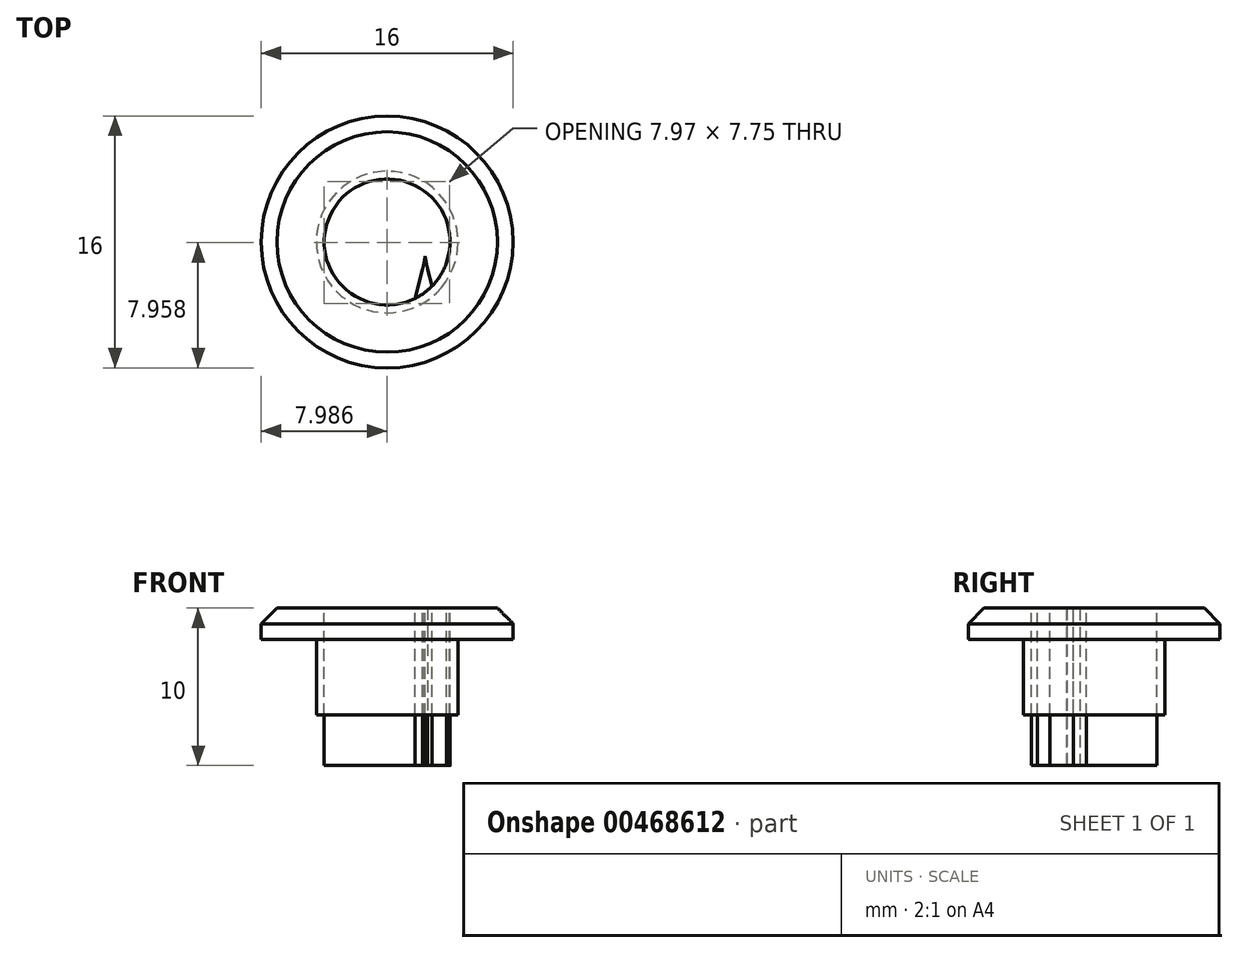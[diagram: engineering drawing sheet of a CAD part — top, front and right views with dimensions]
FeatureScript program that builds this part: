
annotation { "Feature Type Name" : "Feature", "Feature Type Description" : "" }
export const myFeature = defineFeature(function(context is Context, id is Id, definition is map)
    precondition{}
    {
        {
            var Q0;
            Q0=qCreatedBy(makeId("Top.planeOp"),FACE);
            var sketch = newSketch(context, id + "F0", { "sketchPlane" : qUnion([Q0])});
            skCircle(sketch, "E0", {"center": v(0, 0) * mm, "radius": 4 * mm});
            skCircle(sketch, "E1", {"center": v(0, 0) * mm, "radius": 8 * mm});
            skPoint(sketch, "E2", {"position": v(4.15, 5.67) * mm});
            skPoint(sketch, "E3.1.0", {"position": v(-5.11, 4.67) * mm});
            skPoint(sketch, "E3.2.0", {"position": v(-4.11, -4.59) * mm});
            skPoint(sketch, "E3.3.0", {"position": v(5.14, -3.59) * mm});
            skPoint(sketch, "E3.center", {"position": v(0.02, 0.54) * mm});
            skText(sketch, "E4", { "text": "N", "fontName": "OpenSans-Bold.ttf"});
            skText(sketch, "E5", { "text": "W", "fontName": "OpenSans-Bold.ttf"});
            skCircle(sketch, "E6", {"center": v(0, 0) * mm, "radius": 4.5 * mm});
            const initialGuessF0  = {"E4": [-0.00511, 0, 1, 0, 0.00467], "E5": [0, -0.00359, 1, 0, 0.00359]};
            skSetInitialGuess(sketch, initialGuessF0);
            skSolve(sketch);
        }
        {
            var Q0;
            Q0=qSketchRegion(id+"F0",true);
            var Q1;
            {var subQ10=sQuery(id+"F0.wireOp",EDGE,"E5.sketch_text.stroke-0");Q1=makeQuery(id+"F0.imprint","IMPRINT",FACE,{"disambiguationData":[TD([[makeQuery(id+"F0.imprint","IMPRINT",EDGE,{"derivedFrom":subQ10}),-1.0]])]});}
            var Q2;
            {var subQ0=sQuery(id+"F0.wireOp",EDGE,"E5.sketch_text.stroke-18");Q2=makeQuery(id+"F0.imprint","IMPRINT",FACE,{"disambiguationData":[TD([[makeQuery(id+"F0.imprint","IMPRINT",EDGE,{"derivedFrom":subQ0}),1.0]])]});}
            var Q3;
            {var subQ0=sQuery(id+"F0.wireOp",EDGE,"E4.sketch_text.stroke-2");Q3=makeQuery(id+"F0.imprint","IMPRINT",FACE,{"disambiguationData":[TD([[makeQuery(id+"F0.imprint","IMPRINT",EDGE,{"derivedFrom":subQ0}),-1.0]])]});}
            var Q4;
            {var subQ5=sQuery(id+"F0.wireOp",EDGE,"E4.sketch_text.stroke-12");Q4=makeQuery(id+"F0.imprint","IMPRINT",FACE,{"disambiguationData":[TD([[makeQuery(id+"F0.imprint","IMPRINT",EDGE,{"derivedFrom":subQ5}),-1.0]])]});}
            var Q5;
            {var subQ1=sQuery(id+"F0.wireOp",EDGE,"E4.sketch_text.stroke-2");Q5=makeQuery(id+"F0.imprint","IMPRINT",FACE,{"disambiguationData":[TD([[makeQuery(id+"F0.imprint","IMPRINT",EDGE,{"derivedFrom":subQ1}),1.0]])]});}
            extrude(context, id + "F1", {"entities" : qUnion([Q0, Q1, Q2, Q3, Q4, Q5]), "oppositeDirection" : true, "depth" : 2 * mm});
        }
        {
            var Q0;
            {var subQ15=sQuery(id+"F0.wireOp",EDGE,"E4.sketch_text.stroke-0");Q0=makeQuery(id+"F0.imprint","IMPRINT",FACE,{"disambiguationData":[TD([[makeQuery(id+"F0.imprint","IMPRINT",EDGE,{"derivedFrom":subQ15}),1.0]])]});}
            var Q1;
            {var subQ0=sQuery(id+"F0.wireOp",EDGE,"E4.sketch_text.stroke-4");var subQ1=sQuery(id+"F0.wireOp",EDGE,"E0");var subQ2=makeQuery(id+"F0.imprint","INTERSECT",VERTEX,{"derivedFrom":[subQ1,subQ0]});Q1=makeQuery(id+"F0.imprint","IMPRINT",FACE,{"disambiguationData":[TD([[makeQuery(id+"F0.imprint","IMPRINT",EDGE,{"disambiguationData":[TD([[subQ2,-1.0]])],"derivedFrom":subQ1}),1.0]])]});}
            var Q2;
            {var subQ1=sQuery(id+"F0.wireOp",EDGE,"E4.sketch_text.stroke-9");Q2=makeQuery(id+"F0.imprint","IMPRINT",FACE,{"disambiguationData":[TD([[makeQuery(id+"F0.imprint","IMPRINT",EDGE,{"derivedFrom":subQ1}),1.0]])]});}
            var Q3;
            {var subQ5=sQuery(id+"F0.wireOp",EDGE,"E5.sketch_text.stroke-2");Q3=makeQuery(id+"F0.imprint","IMPRINT",FACE,{"disambiguationData":[TD([[makeQuery(id+"F0.imprint","IMPRINT",EDGE,{"derivedFrom":subQ5}),-1.0]])]});}
            var Q4;
            {var subQ0=sQuery(id+"F0.wireOp",EDGE,"E4.sketch_text.stroke-0");Q4=makeQuery(id+"F0.imprint","IMPRINT",FACE,{"disambiguationData":[TD([[makeQuery(id+"F0.imprint","IMPRINT",EDGE,{"derivedFrom":subQ0}),-1.0]])]});}
            extrude(context, id + "F2", {"entities" : qUnion([Q0, Q1, Q2, Q3, Q4]), "operationType" : NewBodyOperationType.ADD, "oppositeDirection" : true, "depth" : 10 * mm});
        }
        {
            var Q0;
            Q0=makeQuery(id+"F1.opExtrude","CAP_EDGE",EDGE,{"disambiguationData":[OSD([sQuery(id+"F0.wireOp",EDGE,"E1")])],"isStart":true});
            chamfer(context, id + "F3", {"entities" : qUnion([Q0]), "width" : 1 * mm, "tangentPropagation" : true});
        }
        {
            var Q0;
            {var subQ0=sQuery(id+"F0.wireOp",EDGE,"E5.sketch_text.stroke-20");Q0=makeQuery(id+"F0.imprint","IMPRINT",FACE,{"disambiguationData":[TD([[makeQuery(id+"F0.imprint","IMPRINT",EDGE,{"derivedFrom":subQ0}),-1.0]])]});}
            var Q1;
            {var subQ0=sQuery(id+"F0.wireOp",EDGE,"E5.sketch_text.stroke-20");Q1=makeQuery(id+"F0.imprint","IMPRINT",FACE,{"disambiguationData":[TD([[makeQuery(id+"F0.imprint","IMPRINT",EDGE,{"derivedFrom":subQ0}),1.0]])]});}
            var Q2;
            {var subQ5=sQuery(id+"F0.wireOp",EDGE,"E0");var subQ7=sQuery(id+"F0.wireOp",EDGE,"E5.sketch_text.stroke-1");var subQ8=makeQuery(id+"F0.imprint","INTERSECT",VERTEX,{"derivedFrom":[subQ5,subQ7]});Q2=makeQuery(id+"F0.imprint","IMPRINT",FACE,{"disambiguationData":[TD([[makeQuery(id+"F0.imprint","IMPRINT",EDGE,{"disambiguationData":[TD([[subQ8,-1.0]])],"derivedFrom":subQ5}),-1.0]])]});}
            var Q3;
            {var subQ0=sQuery(id+"F0.wireOp",EDGE,"E4.sketch_text.stroke-5");var subQ1=sQuery(id+"F0.wireOp",EDGE,"E0");var subQ2=makeQuery(id+"F0.imprint","INTERSECT",VERTEX,{"derivedFrom":[subQ1,subQ0]});Q3=makeQuery(id+"F0.imprint","IMPRINT",FACE,{"disambiguationData":[TD([[makeQuery(id+"F0.imprint","IMPRINT",EDGE,{"disambiguationData":[TD([[subQ2,-1.0]])],"derivedFrom":subQ1}),-1.0]])]});}
            var Q4;
            {var subQ5=sQuery(id+"F0.wireOp",EDGE,"E0");var subQ7=sQuery(id+"F0.wireOp",EDGE,"E4.sketch_text.stroke-13");var subQ8=makeQuery(id+"F0.imprint","INTERSECT",VERTEX,{"derivedFrom":[subQ5,subQ7]});Q4=makeQuery(id+"F0.imprint","IMPRINT",FACE,{"disambiguationData":[TD([[makeQuery(id+"F0.imprint","IMPRINT",EDGE,{"disambiguationData":[TD([[subQ8,1.0]])],"derivedFrom":subQ5}),-1.0]])]});}
            var Q5;
            {var subQ0=sQuery(id+"F0.wireOp",EDGE,"E4.sketch_text.stroke-11");var subQ1=sQuery(id+"F0.wireOp",EDGE,"E0");var subQ2=makeQuery(id+"F0.imprint","INTERSECT",VERTEX,{"derivedFrom":[subQ1,subQ0]});Q5=makeQuery(id+"F0.imprint","IMPRINT",FACE,{"disambiguationData":[TD([[makeQuery(id+"F0.imprint","IMPRINT",EDGE,{"disambiguationData":[TD([[subQ2,1.0]])],"derivedFrom":subQ1}),-1.0]])]});}
            var Q6;
            {var subQ0=sQuery(id+"F0.wireOp",EDGE,"E4.sketch_text.stroke-11");var subQ1=sQuery(id+"F0.wireOp",EDGE,"E0");var subQ2=makeQuery(id+"F0.imprint","INTERSECT",VERTEX,{"derivedFrom":[subQ1,subQ0]});Q6=makeQuery(id+"F0.imprint","IMPRINT",FACE,{"disambiguationData":[TD([[makeQuery(id+"F0.imprint","IMPRINT",EDGE,{"disambiguationData":[TD([[subQ2,-1.0]])],"derivedFrom":subQ1}),-1.0]])]});}
            var Q7;
            {var subQ0=sQuery(id+"F0.wireOp",EDGE,"E4.sketch_text.stroke-8");var subQ1=sQuery(id+"F0.wireOp",EDGE,"E0");var subQ2=makeQuery(id+"F0.imprint","INTERSECT",VERTEX,{"derivedFrom":[subQ1,subQ0]});Q7=makeQuery(id+"F0.imprint","IMPRINT",FACE,{"disambiguationData":[TD([[makeQuery(id+"F0.imprint","IMPRINT",EDGE,{"disambiguationData":[TD([[subQ2,-1.0]])],"derivedFrom":subQ1}),-1.0]])]});}
            var Q8;
            {var subQ1=sQuery(id+"F0.wireOp",EDGE,"E0");var subQ5=sQuery(id+"F0.wireOp",EDGE,"E4.sketch_text.stroke-4");var subQ8=makeQuery(id+"F0.imprint","INTERSECT",VERTEX,{"derivedFrom":[subQ1,subQ5]});Q8=makeQuery(id+"F0.imprint","IMPRINT",FACE,{"disambiguationData":[TD([[makeQuery(id+"F0.imprint","IMPRINT",EDGE,{"disambiguationData":[TD([[subQ8,-1.0]])],"derivedFrom":subQ1}),-1.0]])]});}
            var Q9;
            {var subQ5=sQuery(id+"F0.wireOp",EDGE,"E4.sketch_text.stroke-1");var subQ7=sQuery(id+"F0.wireOp",EDGE,"E0");var subQ9=makeQuery(id+"F0.imprint","INTERSECT",VERTEX,{"derivedFrom":[subQ7,subQ5]});Q9=makeQuery(id+"F0.imprint","IMPRINT",FACE,{"disambiguationData":[TD([[makeQuery(id+"F0.imprint","IMPRINT",EDGE,{"disambiguationData":[TD([[subQ9,-1.0]])],"derivedFrom":subQ7}),-1.0]])]});}
            extrude(context, id + "F4", {"entities" : qUnion([Q0, Q1, Q2, Q3, Q4, Q5, Q6, Q7, Q8, Q9]), "operationType" : NewBodyOperationType.ADD, "oppositeDirection" : true, "depth" : 6.8 * mm});
        }
    });
